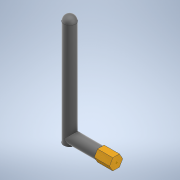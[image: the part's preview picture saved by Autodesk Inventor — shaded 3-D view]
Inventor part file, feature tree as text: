
AUTODESK INVENTOR PART (.ipt)
format: ipt  version: 2020 (Build 240168000, 168)  size: 164,352 bytes
history: native  units: mm
features: extrude x4, sketch x4, other x2, plane x2, fillet x1, projected_geometry x1
ambient origin geometry x8: Origin, YZ Plane, XZ Plane, XY Plane, X Axis, Y Axis, Z Axis, Center Point
bodies: Body1 (feature_tree)
feature tree (14):
  other  "Sólido1"
  extrude  "Extrusión1"  Depth=4.5mm TaperAngle=0.0deg
  fillet  "Empalme1"  Radius=4.5mm
  extrude  "Extrusión2"  Depth=5.196mm
  plane  "Plano de trabajo1"
  plane  "Plano de trabajo2"
  extrude  "Extrusión3"  Depth=5.196mm
  extrude  "Extrusión4"  Depth=12.0mm TaperAngle=0.0deg
  other  "antena"
  sketch  "Boceto1"  dims[d0=9.0mm d1=87.0mm d2=0.0mm d3=4.5mm]
  sketch  "Boceto2"  dims[d9=30.0deg d11=5.196mm]
  projected_geometry  "Contorno proyectado1"
  sketch  "Boceto4"  dims[d12=5.196mm d13=5.196mm]
  sketch  "Boceto5"  dims[d14=5.196mm d15=16.1175mm d16=0.0mm d18=9.0mm d19=4.5mm d20=4.5mm d21=24.5mm d22=0.0mm d26=60.0deg d28=2.598076mm d29=120.0deg d30=12.0mm d31=0.0mm]
